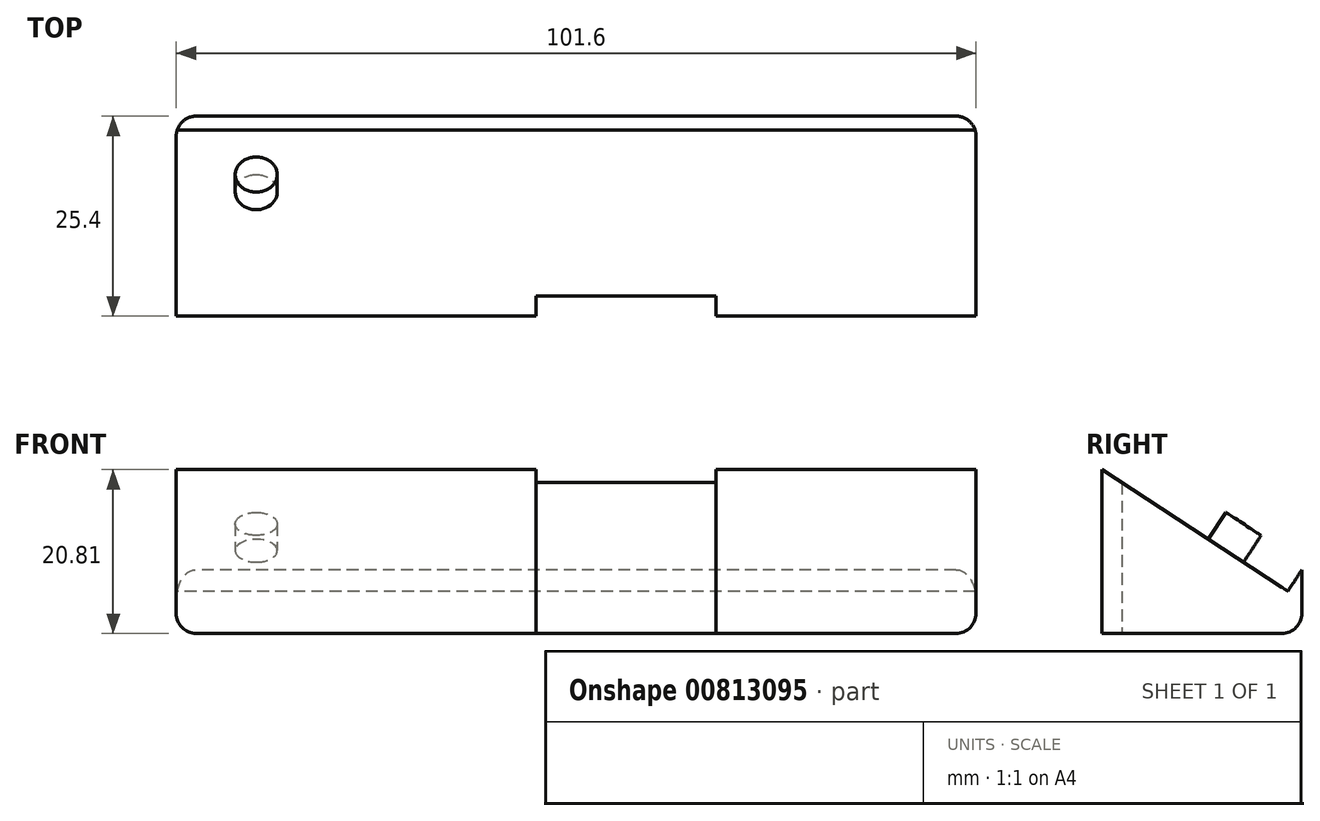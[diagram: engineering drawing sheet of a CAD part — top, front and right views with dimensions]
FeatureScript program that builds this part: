
annotation { "Feature Type Name" : "Feature", "Feature Type Description" : "" }
export const myFeature = defineFeature(function(context is Context, id is Id, definition is map)
    precondition{}
    {
        {
            var Q0;
            Q0=qCreatedBy(makeId("Top.planeOp"),FACE);
            var sketch = newSketch(context, id + "F0", { "sketchPlane" : qUnion([Q0])});
            skLineSegment(sketch, "E0.bottom", {"start": v(-50.8, 12.53) * mm, "end": v(50.8, 12.53) * mm});
            skLineSegment(sketch, "E0.top", {"start": v(-50.8, -12.87) * mm, "end": v(50.8, -12.87) * mm});
            skLineSegment(sketch, "E0.left", {"start": v(-50.8, 12.53) * mm, "end": v(-50.8, -12.87) * mm});
            skLineSegment(sketch, "E0.right", {"start": v(50.8, 12.53) * mm, "end": v(50.8, -12.87) * mm});
            skPoint(sketch, "E1", {"position": v(0, 12.53) * mm});
            skSolve(sketch);
        }
        {
            var Q0;
            Q0=makeQuery(id+"F0.imprint","IMPRINT",FACE,{"disambiguationData":[TD([[makeQuery(id+"F0.imprint","IMPRINT",EDGE,{"derivedFrom":sQuery(id+"F0.wireOp",EDGE,"E0.bottom")}),-1.0]])]});
            extrude(context, id + "F1", {"entities" : qUnion([Q0]), "depth" : 25.4 * mm, "offsetDistance" : 25.4 * mm});
        }
        {
            var Q0;
            Q0=makeQuery(id+"F1.opExtrude","SWEPT_FACE",FACE,{"disambiguationData":[OSD([sQuery(id+"F0.wireOp",EDGE,"E0.left")])]});
            var sketch = newSketch(context, id + "F2", { "sketchPlane" : qUnion([Q0])});
            skLineSegment(sketch, "E2", {"start": v(-12.53, 5.36) * mm, "end": v(12.87, 5.36) * mm, "construction": true});
            skLineSegment(sketch, "E3", {"start": v(-12.53, 8.1) * mm, "end": v(-10.74, 5.36) * mm});
            skLineSegment(sketch, "E4", {"start": v(-10.74, 5.36) * mm, "end": v(12.87, 20.81) * mm});
            skLineSegment(sketch, "E5", {"start": v(-12.53, 8.1) * mm, "end": v(-12.53, 25.4) * mm});
            skLineSegment(sketch, "E6", {"start": v(-12.53, 25.4) * mm, "end": v(12.87, 25.4) * mm});
            skLineSegment(sketch, "E7", {"start": v(12.87, 25.4) * mm, "end": v(12.87, 20.81) * mm});
            skSolve(sketch);
        }
        {
            var Q0;
            Q0=makeQuery(id+"F2.imprint","IMPRINT",FACE,{"disambiguationData":[TD([[makeQuery(id+"F2.imprint","IMPRINT",EDGE,{"derivedFrom":sQuery(id+"F2.wireOp",EDGE,"E3")}),1.0]])]});
            extrude(context, id + "F3", {"entities" : qUnion([Q0]), "operationType" : NewBodyOperationType.REMOVE, "endBound" : BoundingType.UP_TO_NEXT, "oppositeDirection" : true, "depth" : 25.4 * mm, "offsetDistance" : 25.4 * mm});
        }
        {
            var Q0;
            Q0=makeQuery(id+"F1.opExtrude","SWEPT_EDGE",EDGE,{"disambiguationData":[OSD([sQuery(id+"F0.wireOp",EDGE,"E0.bottom"),sQuery(id+"F0.wireOp",EDGE,"E0.right")])]});
            var Q1;
            Q1=makeQuery(id+"F1.opExtrude","CAP_EDGE",EDGE,{"disambiguationData":[OSD([sQuery(id+"F0.wireOp",EDGE,"E0.right")])],"isStart":true});
            var Q2;
            Q2=makeQuery(id+"F1.opExtrude","CAP_EDGE",EDGE,{"disambiguationData":[OSD([sQuery(id+"F0.wireOp",EDGE,"E0.left")])],"isStart":true});
            var Q3;
            Q3=makeQuery(id+"F1.opExtrude","SWEPT_EDGE",EDGE,{"disambiguationData":[OSD([sQuery(id+"F0.wireOp",EDGE,"E0.bottom"),sQuery(id+"F0.wireOp",EDGE,"E0.left")])]});
            var Q4;
            Q4=makeQuery(id+"F1.opExtrude","CAP_EDGE",EDGE,{"disambiguationData":[OSD([sQuery(id+"F0.wireOp",EDGE,"E0.bottom")])],"isStart":true});
            fillet(context, id + "F4", {"entities" : qUnion([Q0, Q1, Q2, Q3, Q4]), "radius" : 2.54 * mm, "tangentPropagation" : true, "allowEdgeOverflow" : false});
        }
        {
            var Q0;
            Q0=makeQuery(id+"F3.boolean.opBoolean","COPY",FACE,{"derivedFrom":makeQuery(id+"F3.opExtrude","SWEPT_FACE",FACE,{"disambiguationData":[OSD([sQuery(id+"F2.wireOp",EDGE,"E4")])]})});
            var sketch = newSketch(context, id + "F5", { "sketchPlane" : qUnion([Q0])});
            skCircle(sketch, "E8", {"center": v(-40.64, -3.34) * mm, "radius": 2.67 * mm});
            skSolve(sketch);
        }
        {
            var Q0;
            Q0=makeQuery(id+"F5.imprint","IMPRINT",FACE,{"disambiguationData":[TD([[makeQuery(id+"F5.imprint","IMPRINT",EDGE,{"derivedFrom":sQuery(id+"F5.wireOp",EDGE,"E8")}),1.0]])]});
            extrude(context, id + "F6", {"entities" : qUnion([Q0]), "operationType" : NewBodyOperationType.ADD, "depth" : 4.06 * mm, "offsetDistance" : 25.4 * mm});
        }
        {
            var Q0;
            Q0=makeQuery(id+"F1.opExtrude","SWEPT_FACE",FACE,{"disambiguationData":[OSD([sQuery(id+"F0.wireOp",EDGE,"E0.top")])]});
            var sketch = newSketch(context, id + "F7", { "sketchPlane" : qUnion([Q0])});
            skLineSegment(sketch, "E9.bottom", {"start": v(-5.08, 20.81) * mm, "end": v(17.78, 20.81) * mm});
            skLineSegment(sketch, "E9.top", {"start": v(-5.08, 0) * mm, "end": v(17.78, 0) * mm});
            skLineSegment(sketch, "E9.left", {"start": v(-5.08, 20.81) * mm, "end": v(-5.08, 0) * mm});
            skLineSegment(sketch, "E9.right", {"start": v(17.78, 20.81) * mm, "end": v(17.78, 0) * mm});
            skSolve(sketch);
        }
        {
            var Q0;
            Q0=makeQuery(id+"F7.imprint","IMPRINT",FACE,{"disambiguationData":[TD([[makeQuery(id+"F7.imprint","IMPRINT",EDGE,{"derivedFrom":sQuery(id+"F7.wireOp",EDGE,"E9.bottom")}),1.0]])]});
            extrude(context, id + "F8", {"entities" : qUnion([Q0]), "operationType" : NewBodyOperationType.REMOVE, "oppositeDirection" : true, "depth" : 2.54 * mm, "offsetDistance" : 25.4 * mm});
        }
    });
